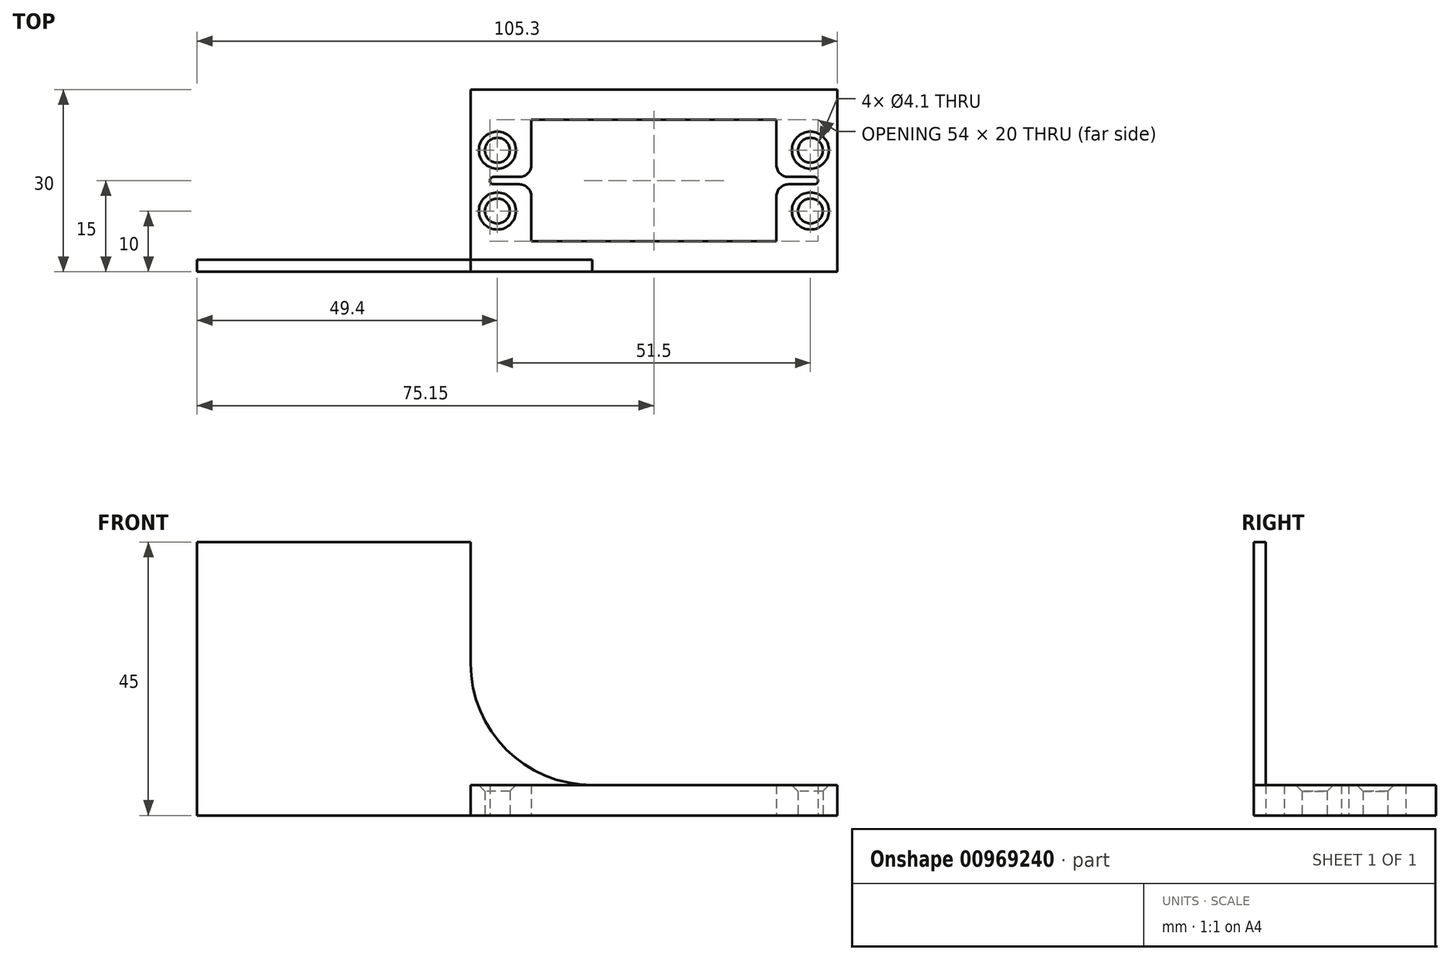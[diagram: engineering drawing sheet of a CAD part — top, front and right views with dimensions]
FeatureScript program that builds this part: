
annotation { "Feature Type Name" : "Feature", "Feature Type Description" : "" }
export const myFeature = defineFeature(function(context is Context, id is Id, definition is map)
    precondition{}
    {
        {
            var Q0;
            Q0=qCreatedBy(makeId("Top.planeOp"),FACE);
            var sketch = newSketch(context, id + "F0", { "sketchPlane" : qUnion([Q0])});
            skLineSegment(sketch, "E0.bottom", {"start": v(30.15, 15) * mm, "end": v(-30.15, 15) * mm});
            skLineSegment(sketch, "E0.top", {"start": v(30.15, -15) * mm, "end": v(-30.15, -15) * mm});
            skLineSegment(sketch, "E0.left", {"start": v(30.15, 15) * mm, "end": v(30.15, -15) * mm});
            skLineSegment(sketch, "E0.right", {"start": v(-30.15, 15) * mm, "end": v(-30.15, -15) * mm});
            skPoint(sketch, "E0.middle", {"position": v(0, 0) * mm});
            skLineSegment(sketch, "E1", {"start": v(0, 10) * mm, "end": v(20.15, 10) * mm});
            skLineSegment(sketch, "E2", {"start": v(20.15, 10) * mm, "end": v(20.15, 2.6) * mm});
            skLineSegment(sketch, "E3", {"start": v(22.15, 0.6) * mm, "end": v(26.4, 0.6) * mm});
            skLineSegment(sketch, "E4", {"start": v(27, 0) * mm, "end": v(27, 0) * mm});
            skPoint(sketch, "E4.endSnap0", {"position": v(30.15, 0) * mm});
            skPoint(sketch, "E5.visualSharp", {"position": v(27, 0.6) * mm});
            skArc(sketch, "E5.filletArc", {"start": v(27, 0) * mm, "mid": v(26.82, 0.42) * mm, "end": v(26.4, 0.6) * mm});
            skPoint(sketch, "E6.visualSharp", {"position": v(20.15, 0.6) * mm});
            skArc(sketch, "E6.filletArc", {"start": v(20.15, 2.6) * mm, "mid": v(20.74, 1.19) * mm, "end": v(22.15, 0.6) * mm});
            skCircle(sketch, "E7", {"center": v(25.75, 5) * mm, "radius": 2.05 * mm});
            skArc(sketch, "E8.MirrorCS", {"start": v(-27, 0) * mm, "mid": v(-26.82, 0.42) * mm, "end": v(-26.4, 0.6) * mm});
            skArc(sketch, "E9.MirrorCS", {"start": v(-20.15, 2.6) * mm, "mid": v(-20.74, 1.19) * mm, "end": v(-22.15, 0.6) * mm});
            skPoint(sketch, "E10.MirrorP", {"position": v(-27, 0.6) * mm});
            skLineSegment(sketch, "E11.MirrorCS", {"start": v(-27, 0) * mm, "end": v(-27, 0) * mm});
            skLineSegment(sketch, "E12.MirrorCS", {"start": v(-20.15, 10) * mm, "end": v(-20.15, 2.6) * mm});
            skCircle(sketch, "E13.MirrorC", {"center": v(-25.75, 5) * mm, "radius": 2.05 * mm});
            skLineSegment(sketch, "E14.MirrorCS", {"start": v(0, 10) * mm, "end": v(-20.15, 10) * mm});
            skPoint(sketch, "E15.MirrorP", {"position": v(-20.15, 0.6) * mm});
            skPoint(sketch, "E16.MirrorP", {"position": v(-30.15, 0) * mm});
            skLineSegment(sketch, "E17.MirrorCS", {"start": v(-22.15, 0.6) * mm, "end": v(-26.4, 0.6) * mm});
            skArc(sketch, "E18.MirrorCS", {"start": v(-27, 0) * mm, "mid": v(-26.82, -0.42) * mm, "end": v(-26.4, -0.6) * mm});
            skArc(sketch, "E19.MirrorCS", {"start": v(27, 0) * mm, "mid": v(26.82, -0.42) * mm, "end": v(26.4, -0.6) * mm});
            skArc(sketch, "E20.MirrorCS", {"start": v(-20.15, -2.6) * mm, "mid": v(-20.74, -1.19) * mm, "end": v(-22.15, -0.6) * mm});
            skArc(sketch, "E21.MirrorCS", {"start": v(20.15, -2.6) * mm, "mid": v(20.74, -1.19) * mm, "end": v(22.15, -0.6) * mm});
            skLineSegment(sketch, "E22.MirrorCS", {"start": v(0, -10) * mm, "end": v(-20.15, -10) * mm});
            skLineSegment(sketch, "E23.MirrorCS", {"start": v(-20.15, -10) * mm, "end": v(-20.15, -2.6) * mm});
            skCircle(sketch, "E24.MirrorC", {"center": v(25.75, -5) * mm, "radius": 2.05 * mm});
            skLineSegment(sketch, "E25.MirrorCS", {"start": v(-22.15, -0.6) * mm, "end": v(-26.4, -0.6) * mm});
            skPoint(sketch, "E26.MirrorP", {"position": v(27, -0.6) * mm});
            skCircle(sketch, "E27.MirrorC", {"center": v(-25.75, -5) * mm, "radius": 2.05 * mm});
            skPoint(sketch, "E28.MirrorP", {"position": v(-20.15, -0.6) * mm});
            skPoint(sketch, "E29.MirrorP", {"position": v(20.15, -0.6) * mm});
            skLineSegment(sketch, "E30.MirrorCS", {"start": v(0, -10) * mm, "end": v(20.15, -10) * mm});
            skLineSegment(sketch, "E31.MirrorCS", {"start": v(20.15, -10) * mm, "end": v(20.15, -2.6) * mm});
            skPoint(sketch, "E32.MirrorP", {"position": v(-27, -0.6) * mm});
            skLineSegment(sketch, "E33.MirrorCS", {"start": v(22.15, -0.6) * mm, "end": v(26.4, -0.6) * mm});
            skSolve(sketch);
        }
        {
            var Q0;
            Q0 = qSketchRegion(id + "F0", true);
            extrude(context, id + "F1", {"entities" : qUnion([Q0]), "depth" : 5 * mm, "offsetDistance" : 25 * mm});
        }
        {
            var Q0;
            Q0=makeQuery(id+"F1.opExtrude","SWEPT_FACE",FACE,{"disambiguationData":[OSD([sQuery(id+"F0.wireOp",EDGE,"E0.top")])]});
            var sketch = newSketch(context, id + "F2", { "sketchPlane" : qUnion([Q0])});
            skLineSegment(sketch, "E34", {"start": v(-30.15, 0) * mm, "end": v(-75.15, 0) * mm});
            skLineSegment(sketch, "E35", {"start": v(-75.15, 0) * mm, "end": v(-75.15, 45) * mm});
            skLineSegment(sketch, "E36", {"start": v(-30.15, 25) * mm, "end": v(-30.15, 45) * mm});
            skLineSegment(sketch, "E37", {"start": v(-75.15, 45) * mm, "end": v(-30.15, 45) * mm});
            skLineSegment(sketch, "E38", {"start": v(-10.15, 5) * mm, "end": v(-10.15, 5) * mm});
            skLineSegment(sketch, "E39", {"start": v(0, 0) * mm, "end": v(-30.15, 0) * mm});
            skPoint(sketch, "E40.visualSharp", {"position": v(-30.15, 5) * mm});
            skArc(sketch, "E40.filletArc", {"start": v(-30.15, 25) * mm, "mid": v(-24.3, 10.86) * mm, "end": v(-10.15, 5) * mm});
            skSolve(sketch);
        }
        {
            var Q0;
            Q0 = qSketchRegion(id + "F2", true);
            var Q1;
            Q1=makeQuery(id+"F2.imprint","IMPRINT",FACE,{"disambiguationData":[TD([[makeQuery(id+"F2.imprint","IMPRINT",EDGE,{"derivedFrom":sQuery(id+"F2.wireOp",EDGE,"E34")}),-1.0]])]});
            extrude(context, id + "F3", {"entities" : qUnion([Q0, Q1]), "oppositeDirection" : true, "depth" : 2 * mm, "offsetDistance" : 25 * mm});
        }
        {
            var Q0;
            Q0=makeQuery(id+"F1.opExtrude","CAP_EDGE",EDGE,{"disambiguationData":[OSD([sQuery(id+"F0.wireOp",EDGE,"E13.MirrorC")])],"isStart":false});
            var Q1;
            Q1=makeQuery(id+"F1.opExtrude","CAP_EDGE",EDGE,{"disambiguationData":[OSD([sQuery(id+"F0.wireOp",EDGE,"E27.MirrorC")])],"isStart":false});
            var Q2;
            Q2=makeQuery(id+"F1.opExtrude","CAP_EDGE",EDGE,{"disambiguationData":[OSD([sQuery(id+"F0.wireOp",EDGE,"E24.MirrorC")])],"isStart":false});
            var Q3;
            Q3=makeQuery(id+"F1.opExtrude","CAP_EDGE",EDGE,{"disambiguationData":[OSD([sQuery(id+"F0.wireOp",EDGE,"E7")])],"isStart":false});
            chamfer(context, id + "F4", {"entities" : qUnion([Q0, Q1, Q2, Q3]), "width" : 1 * mm, "tangentPropagation" : true});
        }
    });
